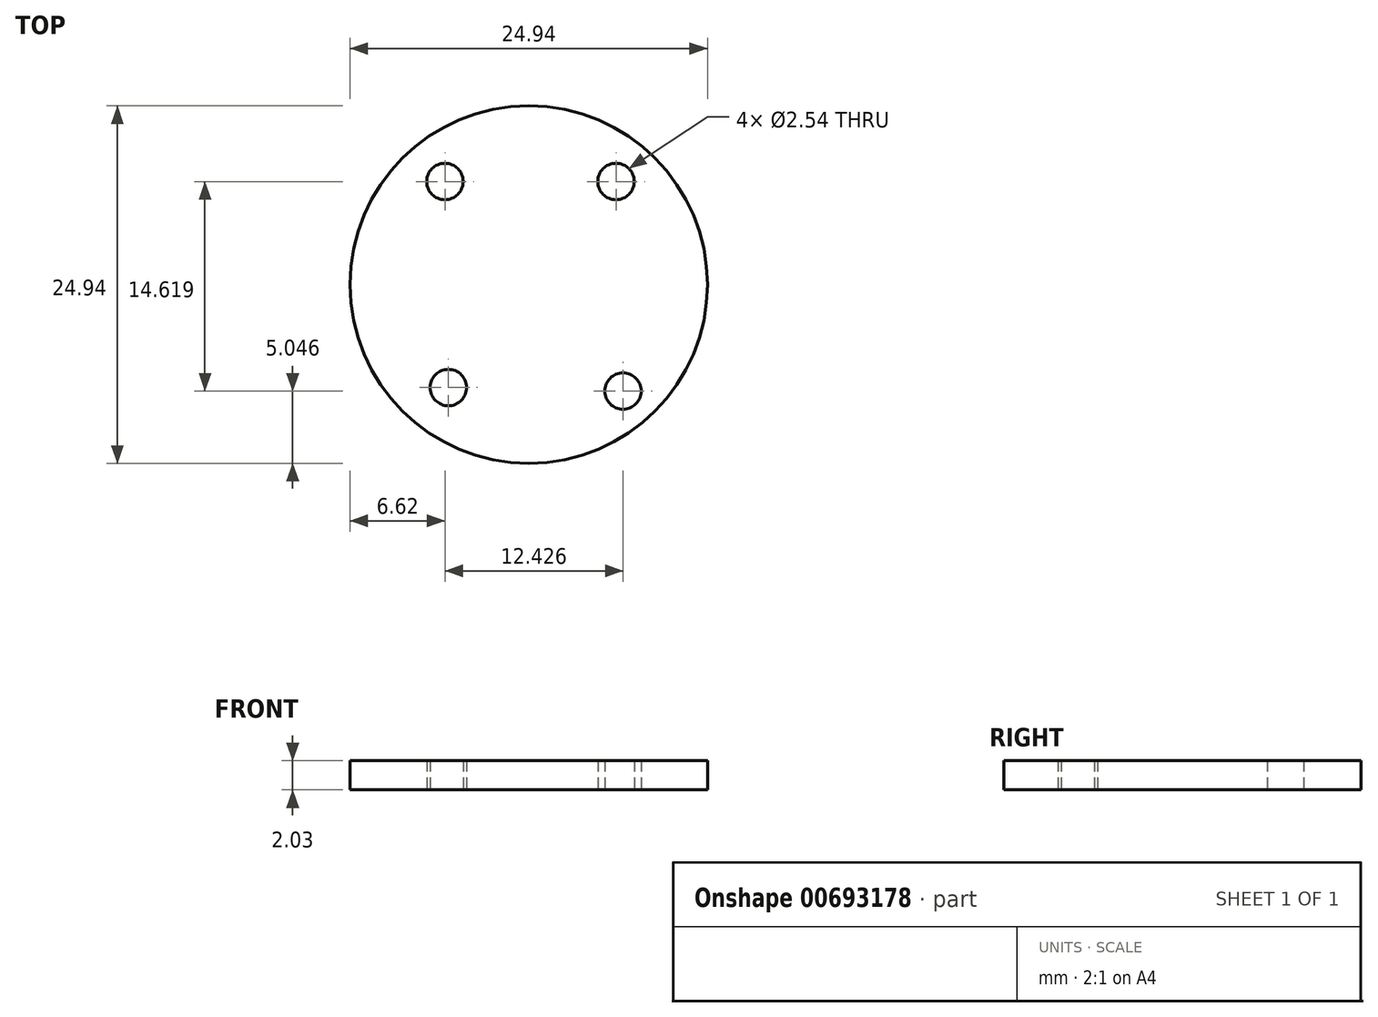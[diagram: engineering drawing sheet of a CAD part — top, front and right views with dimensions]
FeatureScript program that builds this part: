
annotation { "Feature Type Name" : "Feature", "Feature Type Description" : "" }
export const myFeature = defineFeature(function(context is Context, id is Id, definition is map)
    precondition{}
    {
        {
            var Q0;
            Q0=qCreatedBy(makeId("Top.planeOp"),FACE);
            var sketch = newSketch(context, id + "F0", { "sketchPlane" : qUnion([Q0])});
            skCircle(sketch, "E0", {"center": v(0, 0) * mm, "radius": 12.47 * mm});
            skSolve(sketch);
        }
        {
            var Q0;
            Q0=qCreatedBy(makeId("Top.planeOp"),FACE);
            var sketch = newSketch(context, id + "F1", { "sketchPlane" : qUnion([Q0])});
            skCircle(sketch, "E1", {"center": v(-5.85, 7.2) * mm, "radius": 1.32 * mm});
            skCircle(sketch, "E2", {"center": v(-5.6, -7.18) * mm, "radius": 1.32 * mm});
            skCircle(sketch, "E3", {"center": v(6.58, -7.42) * mm, "radius": 1.32 * mm});
            skCircle(sketch, "E4", {"center": v(109.88, -10.84) * mm, "radius": 1.32 * mm});
            skCircle(sketch, "E5", {"center": v(6.09, 7.2) * mm, "radius": 1.32 * mm});
            skCircle(sketch, "E6", {"center": v(124.25, -33.74) * mm, "radius": 1.32 * mm});
            skSolve(sketch);
        }
        {
            var Q0;
            Q0=makeQuery(id+"F0.imprint","IMPRINT",FACE,{"disambiguationData":[TD([[makeQuery(id+"F0.imprint","IMPRINT",EDGE,{"derivedFrom":sQuery(id+"F0.wireOp",EDGE,"E0")}),1.0]])]});
            extrude(context, id + "F2", {"entities" : qUnion([Q0]), "depth" : 2.03 * mm, "offsetDistance" : 25.4 * mm});
        }
        {
            var Q0;
            Q0=sQuery(id+"F1.wireOp",VERTEX,"E2.center");
            var Q1;
            Q1=sQuery(id+"F1.wireOp",VERTEX,"E3.center");
            var Q2;
            Q2=sQuery(id+"F1.wireOp",VERTEX,"E5.center");
            var Q3;
            Q3=sQuery(id+"F1.wireOp",VERTEX,"E1.center");
            var Q4;
            Q4=makeQuery(id+"F2.opExtrude","SWEPT_BODY",BODY,{"disambiguationData":[OSD([sQuery(id+"F0.wireOp",EDGE,"E0")])]});
            hole(context, id + "F3", {"style" : HoleStyle.SIMPLE, "endStyle" : HoleEndStyle.THROUGH, "oppositeDirection" : true, "holeDiameter" : 2.54 * mm, "majorDiameter" : 6.35 * mm, "isTappedThrough" : true, "tappedDepth" : 12.7 * mm, "tapClearance" : 3, "locations" : qUnion([Q0, Q1, Q2, Q3]), "scope" : qUnion([Q4])});
        }
    });
